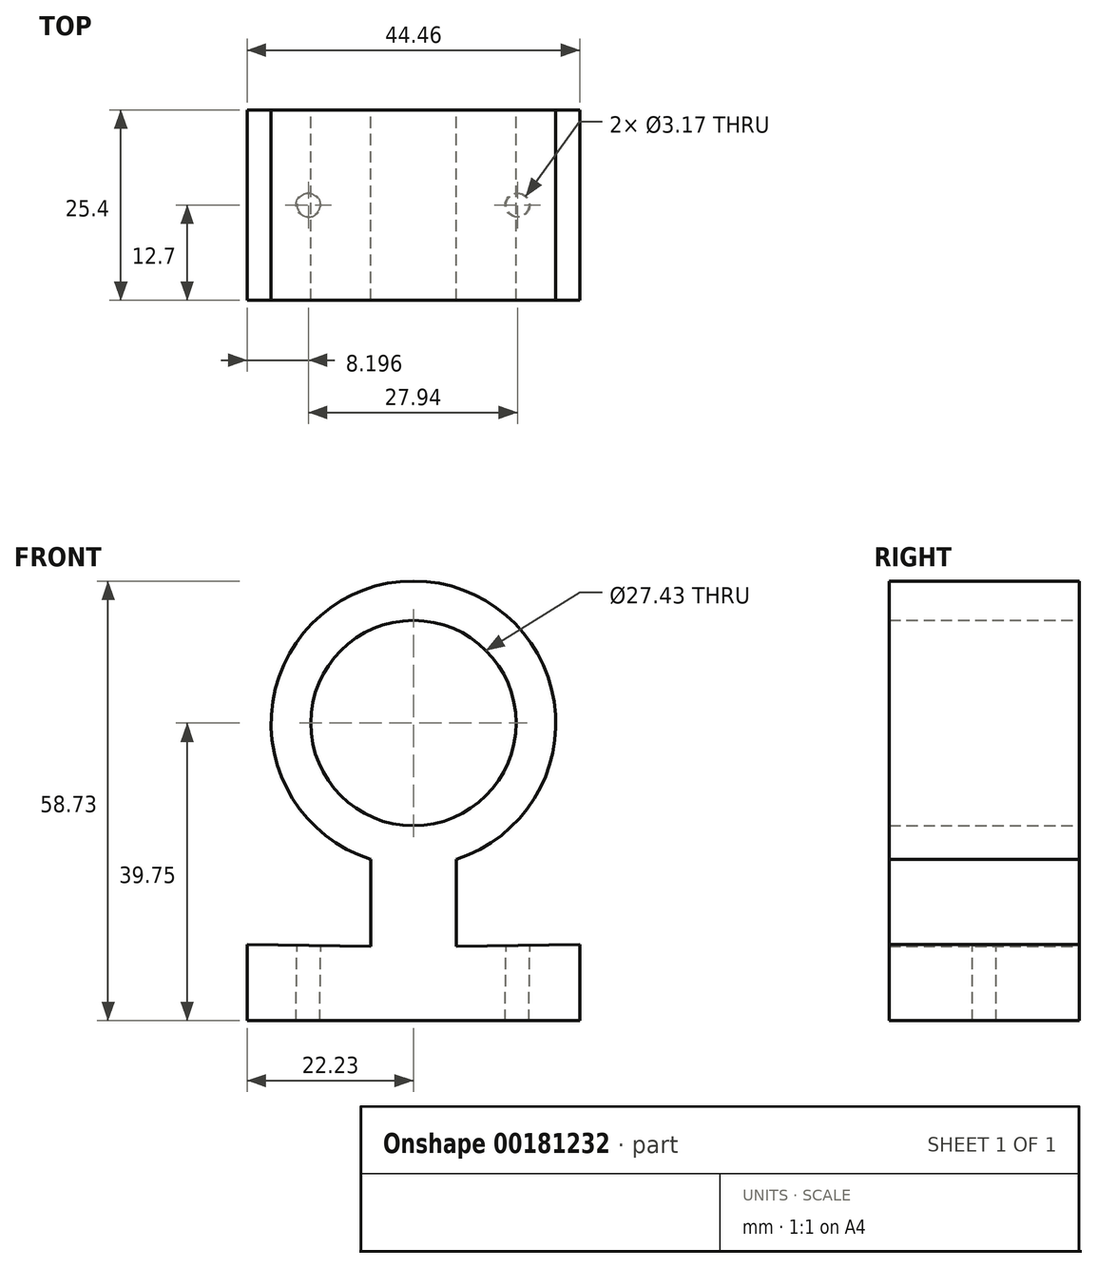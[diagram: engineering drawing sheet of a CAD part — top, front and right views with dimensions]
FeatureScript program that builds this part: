
annotation { "Feature Type Name" : "Feature", "Feature Type Description" : "" }
export const myFeature = defineFeature(function(context is Context, id is Id, definition is map)
    precondition{}
    {
        {
            var Q0;
            Q0=qCreatedBy(makeId("Front.planeOp"),FACE);
            var sketch = newSketch(context, id + "F0", { "sketchPlane" : qUnion([Q0])});
            skCircle(sketch, "E0", {"center": v(0, 0) * mm, "radius": 13.72 * mm});
            skLineSegment(sketch, "E1.left", {"start": v(5.71, -18.17) * mm, "end": v(5.72, -29.8) * mm});
            skLineSegment(sketch, "E1.right", {"start": v(-5.72, -18.17) * mm, "end": v(-5.71, -29.8) * mm});
            skPoint(sketch, "E1.middle", {"position": v(0, -23.98) * mm});
            skLineSegment(sketch, "E2.top", {"start": v(22.23, -39.75) * mm, "end": v(-22.23, -39.75) * mm});
            skLineSegment(sketch, "E2.left", {"start": v(22.23, -29.59) * mm, "end": v(22.23, -39.75) * mm});
            skLineSegment(sketch, "E2.right", {"start": v(-22.23, -29.59) * mm, "end": v(-22.23, -39.75) * mm});
            skPoint(sketch, "E2.middle", {"position": v(0, -34.67) * mm});
            skLineSegment(sketch, "E3", {"start": v(22.23, -29.59) * mm, "end": v(5.72, -29.8) * mm});
            skLineSegment(sketch, "E4", {"start": v(-5.71, -29.8) * mm, "end": v(-22.23, -29.59) * mm});
            skArc(sketch, "E5", {"start": v(5.71, -18.17) * mm, "mid": v(0, 18.98) * mm, "end": v(-5.72, -18.17) * mm});
            skSolve(sketch);
        }
        {
            var Q0;
            Q0=makeQuery(id+"F0.imprint","IMPRINT",FACE,{"disambiguationData":[TD([[makeQuery(id+"F0.imprint","IMPRINT",EDGE,{"derivedFrom":sQuery(id+"F0.wireOp",EDGE,"E0")}),-1.0]])]});
            extrude(context, id + "F1", {"entities" : qUnion([Q0]), "depth" : 25.4 * mm});
        }
        {
            var Q0;
            Q0=makeQuery(id+"F1.opExtrude","SWEPT_FACE",FACE,{"disambiguationData":[OSD([sQuery(id+"F0.wireOp",EDGE,"E3")])]});
            var sketch = newSketch(context, id + "F2", { "sketchPlane" : qUnion([Q0])});
            skCircle(sketch, "E6", {"center": v(13.6, -12.7) * mm, "radius": 1.59 * mm});
            skSolve(sketch);
        }
        {
            var Q0;
            Q0=makeQuery(id+"F1.opExtrude","SWEPT_FACE",FACE,{"disambiguationData":[OSD([sQuery(id+"F0.wireOp",EDGE,"E4")])]});
            var sketch = newSketch(context, id + "F3", { "sketchPlane" : qUnion([Q0])});
            skCircle(sketch, "E7", {"center": v(-13.6, -12.7) * mm, "radius": 1.59 * mm});
            skSolve(sketch);
        }
        {
            var Q0;
            Q0 = qSketchRegion(id + "F3", true);
            var Q1;
            Q1=makeQuery(id+"F2.imprint","IMPRINT",FACE,{"disambiguationData":[TD([[makeQuery(id+"F2.imprint","IMPRINT",EDGE,{"derivedFrom":sQuery(id+"F2.wireOp",EDGE,"E6")}),1.0]])]});
            extrude(context, id + "F4", {"entities" : qUnion([Q0, Q1]), "operationType" : NewBodyOperationType.REMOVE, "oppositeDirection" : true, "depth" : 25.4 * mm});
        }
    });
